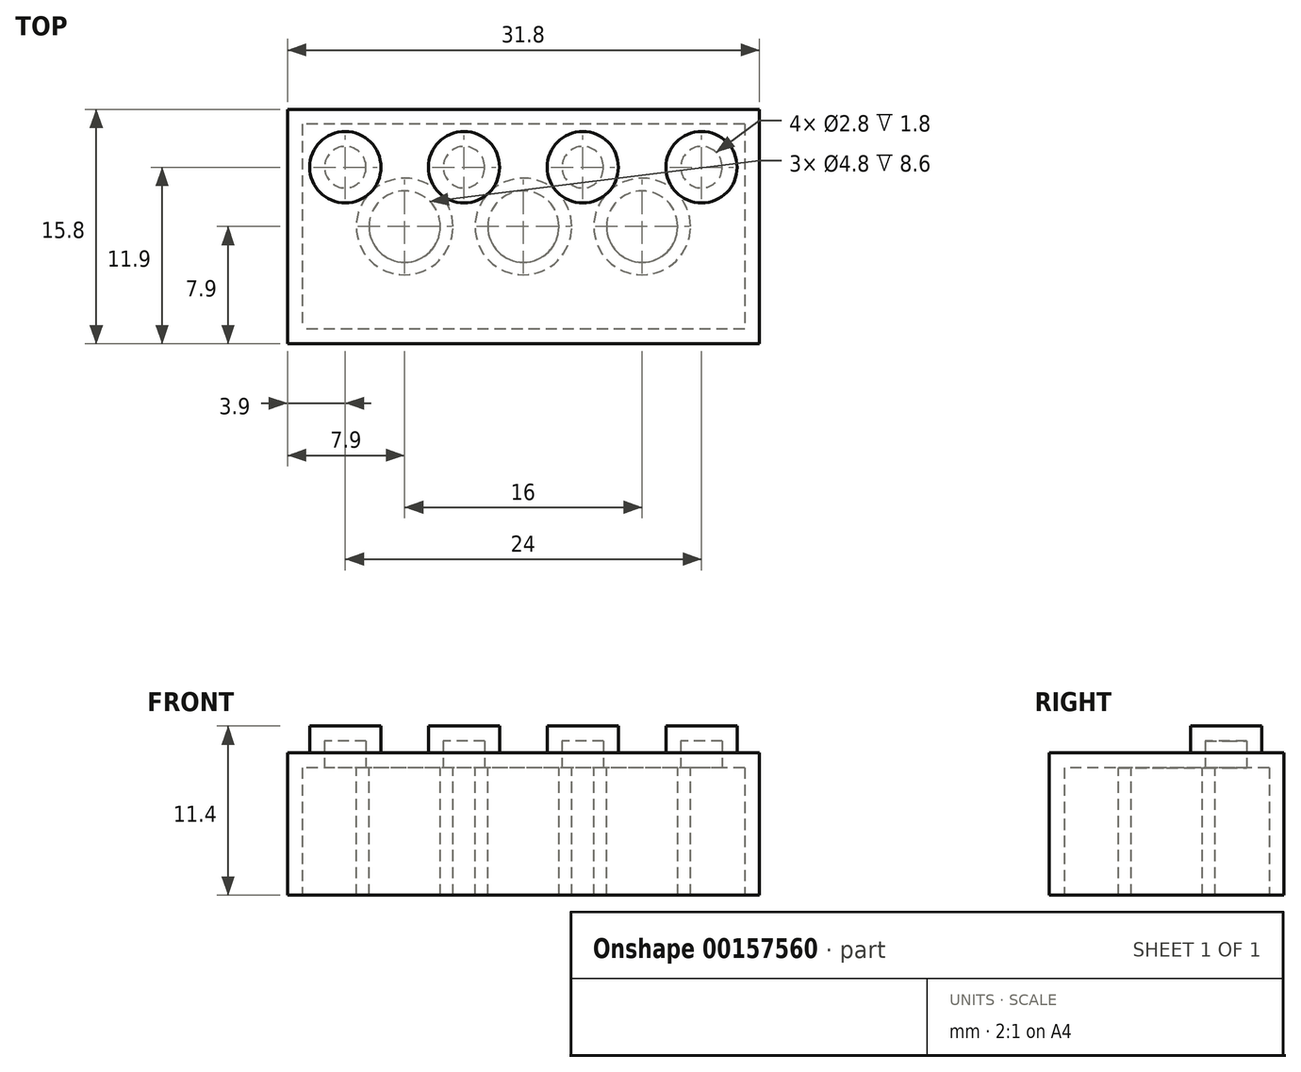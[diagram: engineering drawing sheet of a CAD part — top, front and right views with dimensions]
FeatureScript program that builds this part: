
annotation { "Feature Type Name" : "Feature", "Feature Type Description" : "" }
export const myFeature = defineFeature(function(context is Context, id is Id, definition is map)
    precondition{}
    {
        {
            var Q0;
            Q0=qCreatedBy(makeId("Top.planeOp"),FACE);
            var sketch = newSketch(context, id + "F0", { "sketchPlane" : qUnion([Q0])});
            skLineSegment(sketch, "E0.bottom", {"start": v(15.9, 7.9) * mm, "end": v(-15.9, 7.9) * mm});
            skLineSegment(sketch, "E0.top", {"start": v(15.9, -7.9) * mm, "end": v(-15.9, -7.9) * mm});
            skLineSegment(sketch, "E0.left", {"start": v(15.9, 7.9) * mm, "end": v(15.9, -7.9) * mm});
            skLineSegment(sketch, "E0.right", {"start": v(-15.9, 7.9) * mm, "end": v(-15.9, -7.9) * mm});
            skPoint(sketch, "E0.middle", {"position": v(0, 0) * mm});
            skSolve(sketch);
        }
        {
            var Q0;
            Q0 = qSketchRegion(id + "F0", true);
            extrude(context, id + "F1", {"entities" : qUnion([Q0]), "depth" : 9.6 * mm});
        }
        {
            var Q0;
            Q0=makeQuery(id+"F1.opExtrude","CAP_FACE",FACE,{"disambiguationData":[OSD([sQuery(id+"F0.wireOp",EDGE,"E0.bottom"),sQuery(id+"F0.wireOp",EDGE,"E0.top"),sQuery(id+"F0.wireOp",EDGE,"E0.left"),sQuery(id+"F0.wireOp",EDGE,"E0.right")])],"isStart":false});
            var sketch = newSketch(context, id + "F2", { "sketchPlane" : qUnion([Q0])});
            skCircle(sketch, "E1", {"center": v(-12, 4) * mm, "radius": 2.4 * mm});
            skLineSegment(sketch, "E2", {"start": v(-12, 4) * mm, "end": v(-15.9, 4) * mm, "construction": true});
            skLineSegment(sketch, "E3", {"start": v(-12, 4) * mm, "end": v(-12, 7.9) * mm, "construction": true});
            skCircle(sketch, "E4.1.0.0", {"center": v(-4, 4) * mm, "radius": 2.4 * mm});
            skCircle(sketch, "E4.2.0.0", {"center": v(4, 4) * mm, "radius": 2.4 * mm});
            skCircle(sketch, "E4.3.0.0", {"center": v(12, 4) * mm, "radius": 2.4 * mm});
            skLineSegment(sketch, "E4.direction1", {"start": v(-12, 4) * mm, "end": v(-4, 4) * mm, "construction": true});
            skLineSegment(sketch, "E5", {"start": v(12, 4) * mm, "end": v(15.9, 4) * mm, "construction": true});
            skSolve(sketch);
        }
        {
            var Q0;
            Q0 = qSketchRegion(id + "F2", true);
            extrude(context, id + "F3", {"entities" : qUnion([Q0]), "operationType" : NewBodyOperationType.ADD, "depth" : 1.8 * mm});
        }
        {
            var Q0;
            Q0=makeQuery(id+"F1.opExtrude","CAP_FACE",FACE,{"disambiguationData":[OSD([sQuery(id+"F0.wireOp",EDGE,"E0.bottom"),sQuery(id+"F0.wireOp",EDGE,"E0.top"),sQuery(id+"F0.wireOp",EDGE,"E0.left"),sQuery(id+"F0.wireOp",EDGE,"E0.right")])],"isStart":true});
            shell(context, id + "F4", {"entities" : qUnion([Q0]), "thickness" : 1 * mm});
        }
        {
            var Q0;
            Q0=makeQuery(id+"F4.opShell","OFFSET_FACE",FACE,{"disambiguationData":[OSD([sQuery(id+"F0.wireOp",EDGE,"E0.bottom"),sQuery(id+"F0.wireOp",EDGE,"E0.top"),sQuery(id+"F0.wireOp",EDGE,"E0.left"),sQuery(id+"F0.wireOp",EDGE,"E0.right")])]});
            var sketch = newSketch(context, id + "F5", { "sketchPlane" : qUnion([Q0])});
            skLineSegment(sketch, "E6", {"start": v(-4, 4) * mm, "end": v(-12, -4) * mm, "construction": true});
            skLineSegment(sketch, "E7", {"start": v(-4, -4) * mm, "end": v(-12, 4) * mm, "construction": true});
            skCircle(sketch, "E8", {"center": v(-8, 0) * mm, "radius": 2.4 * mm});
            skCircle(sketch, "E9", {"center": v(-8, 0) * mm, "radius": 3.25 * mm});
            skCircle(sketch, "E10.1.0.0", {"center": v(0, 0) * mm, "radius": 3.25 * mm});
            skCircle(sketch, "E10.1.0.1", {"center": v(0, 0) * mm, "radius": 2.4 * mm});
            skCircle(sketch, "E10.2.0.0", {"center": v(8, 0) * mm, "radius": 3.25 * mm});
            skCircle(sketch, "E10.2.0.1", {"center": v(8, 0) * mm, "radius": 2.4 * mm});
            skLineSegment(sketch, "E10.direction1", {"start": v(-8, 0) * mm, "end": v(0, 0) * mm, "construction": true});
            skSolve(sketch);
        }
        {
            var Q0;
            Q0 = qSketchRegion(id + "F5", true);
            var Q1;
            Q1=makeQuery(id+"F1.opExtrude","CAP_FACE",FACE,{"disambiguationData":[OSD([sQuery(id+"F0.wireOp",EDGE,"E0.bottom"),sQuery(id+"F0.wireOp",EDGE,"E0.top"),sQuery(id+"F0.wireOp",EDGE,"E0.left"),sQuery(id+"F0.wireOp",EDGE,"E0.right")])],"isStart":true});
            extrude(context, id + "F6", {"entities" : qUnion([Q0]), "operationType" : NewBodyOperationType.ADD, "endBound" : BoundingType.UP_TO_SURFACE, "endBoundEntityFace" : qUnion([Q1]), "depth" : 25 * mm});
        }
    });
